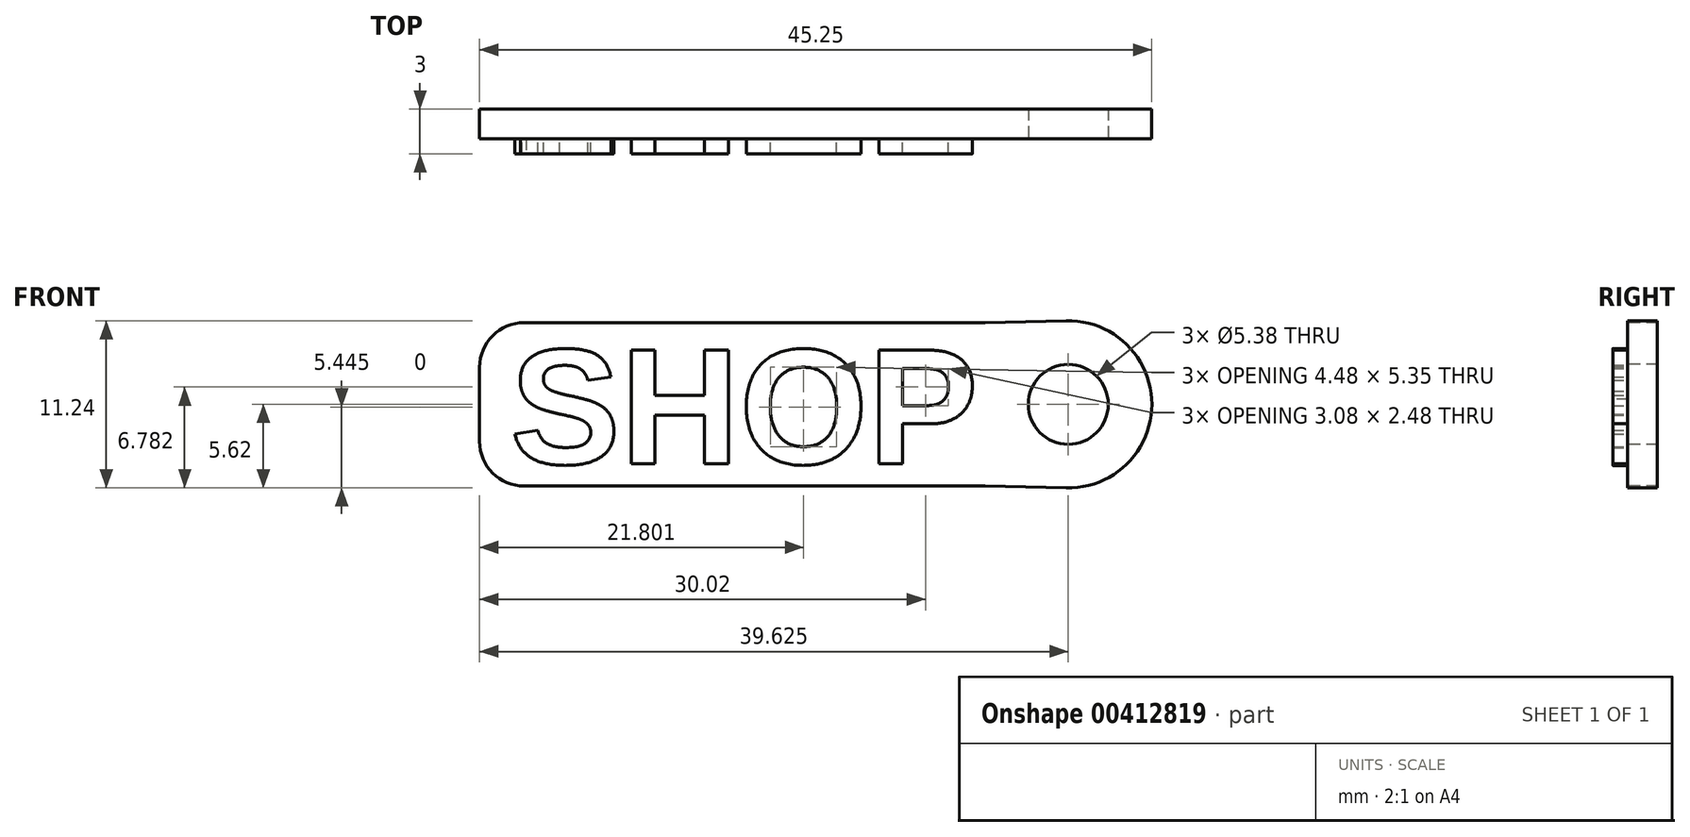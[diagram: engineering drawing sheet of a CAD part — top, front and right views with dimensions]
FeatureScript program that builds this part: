
annotation { "Feature Type Name" : "Feature", "Feature Type Description" : "" }
export const myFeature = defineFeature(function(context is Context, id is Id, definition is map)
    precondition{}
    {
        {
            var Q0;
            Q0=qCreatedBy(makeId("Front.planeOp"),FACE);
            var sketch = newSketch(context, id + "F0", { "sketchPlane" : qUnion([Q0])});
            skText(sketch, "E0", { "text": "SHOP", "fontName": "Arimo-Bold.ttf"});
            const initialGuessF0  = {"E0": [-0.01594, -0.008, 1, 0, 0.008]};
            skSetInitialGuess(sketch, initialGuessF0);
            skSolve(sketch);
        }
        {
            var Q0;
            Q0=qSketchRegion(id+"F0",true);
            extrude(context, id + "F1", {"entities" : qUnion([Q0]), "depth" : 1 * mm});
        }
        {
            var Q0;
            Q0=qCreatedBy(makeId("Front.planeOp"),FACE);
            var sketch = newSketch(context, id + "F2", { "sketchPlane" : qUnion([Q0])});
            skLineSegment(sketch, "E1", {"start": v(16, -9.5) * mm, "end": v(-18, -9.5) * mm});
            skLineSegment(sketch, "E2", {"start": v(-18, 1.5) * mm, "end": v(16, 1.5) * mm});
            skLineSegment(sketch, "E3", {"start": v(16, -9.5) * mm, "end": v(16, 1.5) * mm, "construction": true});
            skLineSegment(sketch, "E4", {"start": v(-18, -9.5) * mm, "end": v(-18, 1.5) * mm});
            skCircle(sketch, "E5", {"center": v(21.62, -4) * mm, "radius": 5.62 * mm});
            skLineSegment(sketch, "E6", {"start": v(16, -4) * mm, "end": v(67.35, -4) * mm, "construction": true});
            skPoint(sketch, "E6.endSnap0", {"position": v(16, -4) * mm});
            skLineSegment(sketch, "E7", {"start": v(16, 1.5) * mm, "end": v(21.5, 1.62) * mm});
            skLineSegment(sketch, "E8", {"start": v(21.5, -9.62) * mm, "end": v(16, -9.5) * mm});
            skCircle(sketch, "E9", {"center": v(21.62, -4) * mm, "radius": 2.69 * mm});
            skSolve(sketch);
        }
        {
            var Q0;
            Q0=qSketchRegion(id+"F2",true);
            extrude(context, id + "F3", {"entities" : qUnion([Q0]), "oppositeDirection" : true, "depth" : 2 * mm});
        }
        {
            var Q0;
            Q0=makeQuery(id+"F3.opExtrude","SWEPT_EDGE",EDGE,{"disambiguationData":[OSD([sQuery(id+"F2.wireOp",EDGE,"E2"),sQuery(id+"F2.wireOp",EDGE,"E4")])]});
            var Q1;
            Q1=makeQuery(id+"F3.opExtrude","SWEPT_EDGE",EDGE,{"disambiguationData":[OSD([sQuery(id+"F2.wireOp",EDGE,"E1"),sQuery(id+"F2.wireOp",EDGE,"E4")])]});
            var Q2;
            Q2=makeQuery(id+"F3.opExtrude","SWEPT_EDGE",EDGE,{"disambiguationData":[OSD([sQuery(id+"F2.wireOp",EDGE,"E1"),sQuery(id+"F2.wireOp",EDGE,"E8")])]});
            var Q3;
            Q3=makeQuery(id+"F3.opExtrude","SWEPT_EDGE",EDGE,{"disambiguationData":[OSD([sQuery(id+"F2.wireOp",EDGE,"E2"),sQuery(id+"F2.wireOp",EDGE,"E7")])]});
            fillet(context, id + "F4", {"entities" : qUnion([Q0, Q1, Q2, Q3]), "radius" : 3 * mm, "tangentPropagation" : true, "allowEdgeOverflow" : false});
        }
    });
